# Revit family: IS_ConnectAir_E1069_BIM_DE
name_source: partatom
category: Plumbing Fixtures
revit_build: Autodesk Revit MEP 2014 (Build: 20130308_1515(x64)
units: mm (PartAtom-declared; Revit-internal decimal feet)

## types (1)
- E106901 - Connect Air hexagon bath tub
    Accessories = www.idealstandard.de\ersatzteile
    AreaUnits = millimeters
    Assembly Code = C1030200
    AssetType = Fixed
    BIMObjectName = ISI_IdealStandard_Baths_ConnectAir_E106901
    BarCode = 5017830518785
    BathType = Domestic
    Brand = Ideal Standard
    Category = SanitaryTerminal_BATH_DE
    CodePerformance = DIN EN 14516, DIN EN 232, DIN EN 198
    Color = white
    ConnectionType = Plumbing
    Default Elevation = 610 mm
    Description = E106901 Connect Air hexagon bath tub
    DrainSize = 52 mm
    DurationUnit = year
    ExpectedLife = 25
    Features = Connect Air hexagon bath tub
    Finish = white
    GrossWeight = 0
    HasGrabHandles = No
    IfcExportAs = IfcSanitaryTerminalType
    IfcExportType = BATH
    InstallationInstructions = www.idealstandard.de\produkte
    LinearUnits = millimeters
    ManufacturerURL = www.idealstandard.de
    Material = Sanitary Brass
    MaterialThickness = 4 mm  [stored 0.0131234 ft]
    Model = E106901
    ModelNumber = E106901
    ModelReference = E106901 Connect Air hexagon bath tub
    NBSDescription = Baths
    NBSReference = 45-35-70/311
    Name = Baths_ConnectAir_E106901_IdealStandard
    NettWeight = 25 kg
    NominalDepth = 900 mm
    NominalHeight = 465 mm
    NominalLength = 900 mm
    NominalWidth = 1900 mm
    ProductInformation = www.idealstandard.de/produkte
    Shape = Hexagon
    Size = 1900x800x40mm
    Space = Internal
    SpareParts = www.idealstandard.de/ersatzteile
    TMV3 = No
    URL = www.idealstandard.com
    Uniclass2015Code = Pr_40_20_06_08
    Uniclass2015Title = Baths
    Uniclass2015Version = Products v1.1
    Version = 1
    VolumeUnits = Litres
    WarrantyDescription = Manufacturers Warranty
    WarrantyDurationUnit = year

note: [stored X ft] marks values corroborated as IEEE doubles in the binary element streams (Revit-internal decimal feet)

## geometry (parser evidence)
native form markers: Sweep x2
no freeform markers — native parametric forms only
